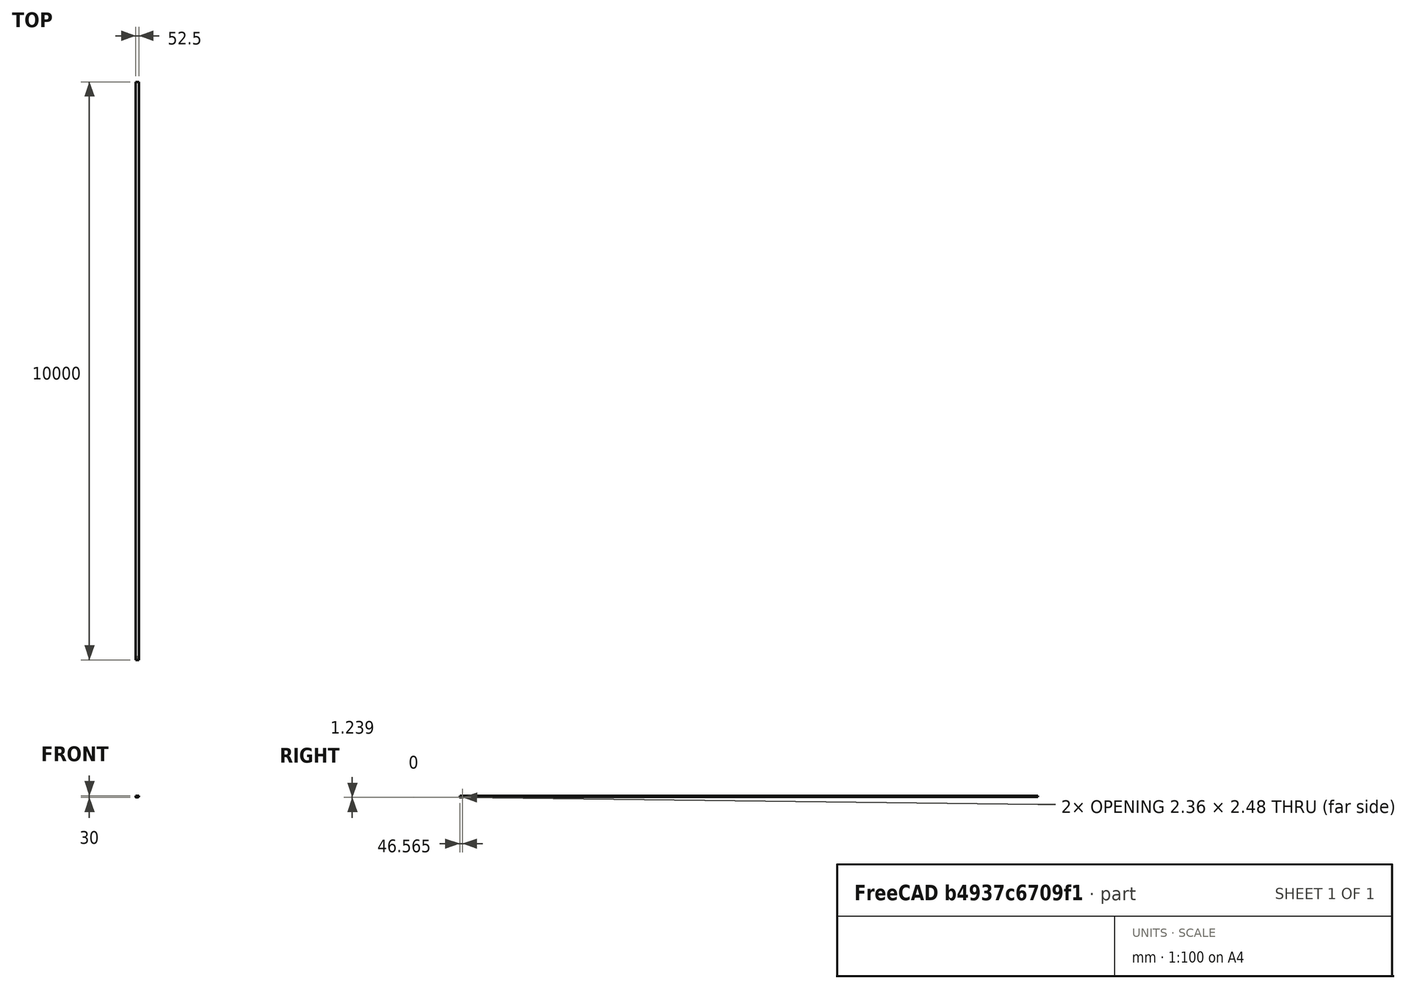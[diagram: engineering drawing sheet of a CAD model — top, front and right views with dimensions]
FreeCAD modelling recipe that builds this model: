
FCSTD DOCUMENT  (FreeCAD 0.14R3700 (Git))
Label: Phone_stand_flippable_stand
License: CC-BY 3.0
LicenseURL: http://creativecommons.org/licenses/by/3.0/
objects: Sketcher::SketchObject×4, PartDesign::Pad×2, PartDesign::Pocket×2, PartDesign::Fillet×1, Mesh::Feature×1
note: 13 computed .brp shape members not serialized (recipe doc carries the construction recipe); baked Part::Feature solids carry a one-line shape summary decoded from their .brp

FEATURE [Sketcher::SketchObject] Sketch001  label="X-Section"
  Placement = pos=(0,0,0) rot=(0.57735,0.57735,0.57735;2.0944rad)
  sketch-geometry (13):
    g0: LineSegment StartX=1.5 StartY=0 StartZ=0 EndX=58 EndY=0 EndZ=0
    g1: LineSegment StartX=58 StartY=4 StartZ=0 EndX=5.5 EndY=4 EndZ=0
    g2: LineSegment StartX=0 StartY=16.2 StartZ=0 EndX=0 EndY=1.5 EndZ=0
    g3: LineSegment StartX=1.5 StartY=17.7 StartZ=0 EndX=6.23478 EndY=17.7 EndZ=0
    g4: ArcOfCircle CenterX=1.5 CenterY=1.5 CenterZ=0 NormalX=0 NormalY=0 NormalZ=1 Radius=1.5 StartAngle=3.14159 EndAngle=4.71239
    g5: ArcOfCircle CenterX=1.5 CenterY=16.2 CenterZ=0 NormalX=0 NormalY=0 NormalZ=1 Radius=1.5 StartAngle=1.5708 EndAngle=3.14159
    g6: LineSegment StartX=4 StartY=5.5 StartZ=0 EndX=4 EndY=12.8 EndZ=0
    g7: ArcOfCircle CenterX=6.23116 CenterY=12.8 CenterZ=0 NormalX=0 NormalY=0 NormalZ=1 Radius=2.23116 StartAngle=2.27529 EndAngle=3.14159
    g8: LineSegment StartX=4.78615 StartY=14.5 StartZ=0 EndX=6.78615 EndY=16.2 EndZ=0
    g9: ArcOfCircle CenterX=6.23478 CenterY=16.8487 CenterZ=0 NormalX=0 NormalY=0 NormalZ=1 Radius=0.851335 StartAngle=5.41688 EndAngle=7.85398
    g10: LineSegment [constr] StartX=0 StartY=16.2 StartZ=0 EndX=6.78615 EndY=16.2 EndZ=0
    g11: LineSegment StartX=58 StartY=4 StartZ=0 EndX=58 EndY=0 EndZ=0
    g12: ArcOfCircle CenterX=5.5 CenterY=5.5 CenterZ=0 NormalX=0 NormalY=0 NormalZ=1 Radius=1.5 StartAngle=3.14159 EndAngle=4.71239
  constraints (36):
    c: Horizontal(g0)
    c: Horizontal(g1)
    c: Vertical(g2)
    c: Horizontal(g3)
    c: Tangent(g2,g4)
    c: Tangent(g0,g4)
    c: Tangent(g2,g5)
    c: Tangent(g3,g5)
    c: PointOnObject(g2,g-2)
    c: Vertical(g6)
    c: Coincident(g7,g6)
    c: Tangent(g7,g6)
    c: Coincident(g8,g7)
    c: Tangent(g8,g7)
    c: Tangent(g8,g9)
    c: Coincident(g9,g3)
    c: Tangent(g3,g9)
    c: Coincident(g10,g2)
    c: Coincident(g10,g8)
    c: Horizontal(g10)
    c: Radius(g4) = 1.5
    c: Radius(g5) = 1.5
    c: PointOnObject(g0,g-1)
    c: DistanceX(g7,g8) = 2
    c: Coincident(g11,g1)
    c: Coincident(g11,g0)
    c: Vertical(g11)
    c: DistanceY(g11) = -4
    c: DistanceX(g2,g0) = 58
    c: Tangent(g1,g12)
    c: Tangent(g6,g12)
    c: DistanceX(g6,g2) = -4
    c: DistanceY(g6,g1) = -8.8
    c: DistanceY(g7,g1) = -10.5
    c: DistanceY(g8,g1) = -12.2
    c: Radius(g12) = 1.5
FEATURE [PartDesign::Pad] Pad
  Length = 40
  Length2 = 100
  Placement = pos=(0,0,0) rot=(0.57735,0.57735,0.57735;2.0944rad)
  Sketch = -> Sketch001
  Type = 0
FEATURE [Sketcher::SketchObject] Sketch  label="Centre-Pocket"
  ExternalGeometry = -> [Pad]
  Placement = pos=(0,0,0) rot=(0.707107,0.707107,0;3.14159rad)
  Support = -> Pad [Face4]
  sketch-geometry (7):
    g0: LineSegment StartX=0 StartY=30 StartZ=0 EndX=52.5 EndY=30 EndZ=0
    g1: LineSegment StartX=52.5 StartY=30 StartZ=0 EndX=52.5 EndY=10 EndZ=0
    g2: LineSegment StartX=52.5 StartY=10 StartZ=0 EndX=0 EndY=10 EndZ=0
    g3: LineSegment StartX=0 StartY=10 StartZ=0 EndX=0 EndY=30 EndZ=0
    g4: LineSegment [constr] StartX=0 StartY=20 StartZ=0 EndX=58 EndY=20 EndZ=0
    g5: LineSegment [constr] StartX=1.5 StartY=40 StartZ=0 EndX=46.5 EndY=40 EndZ=0
    g6: LineSegment [constr] StartX=46.5 StartY=40 StartZ=0 EndX=52.5 EndY=40 EndZ=0
  constraints (20):
    c: Coincident(g0,g1)
    c: Coincident(g1,g2)
    c: Coincident(g2,g3)
    c: Coincident(g3,g0)
    c: Horizontal(g0)
    c: Horizontal(g2)
    c: Vertical(g1)
    c: Vertical(g3)
    c: Symmetric(g0,g2,g4)
    c: PointOnObject(g4,g-2)
    c: DistanceY(g3) = 20
    c: PointOnObject(g4,g3)
    c: Horizontal(g5)
    c: DistanceX(g5) = 45
    c: Symmetric(g-3,g-3,g4)
    c: Coincident(g6,g5)
    c: Horizontal(g6)
    c: DistanceX(g6) = 6
    c: PointOnObject(g6,g1)
    c: Coincident(g5,g-4)
FEATURE [PartDesign::Pocket] Pocket
  Length = 5
  Placement = pos=(0,0,0) rot=(0.57735,0.57735,0.57735;2.0944rad)
  Sketch = -> Sketch
  Type = 1
FEATURE [Sketcher::SketchObject] Sketch002  label="Centre-Hinge-X-Section"
  ExternalGeometry = -> [Pocket]
  Placement = pos=(10,0,0) rot=(0.57735,0.57735,0.57735;2.0944rad)
  Support = -> Pocket [Face4]
  sketch-geometry (12):
    g0: LineSegment [constr] StartX=1.5 StartY=1.5 StartZ=0 EndX=46.5 EndY=1.5 EndZ=0
    g1: LineSegment StartX=52.5 StartY=4 StartZ=0 EndX=51 EndY=4 EndZ=0
    g2: LineSegment StartX=52.5 StartY=4 StartZ=0 EndX=52.5 EndY=0 EndZ=0
    g3: LineSegment StartX=52.5 StartY=0 StartZ=0 EndX=51.866 EndY=0 EndZ=0
    g4: LineSegment StartX=51 StartY=4 StartZ=0 EndX=51 EndY=1.5 EndZ=0
    g5: LineSegment StartX=51 StartY=1.5 StartZ=0 EndX=51.866 EndY=0 EndZ=0
    g6: ArcOfCircle CenterX=1.5 CenterY=1.5 CenterZ=0 NormalX=0 NormalY=0 NormalZ=1 Radius=1.5 StartAngle=2.15007 EndAngle=6.75111
    g7: LineSegment StartX=0.678881 StartY=2.75529 StartZ=0 EndX=2.83876 EndY=2.17656 EndZ=0
    g8: ArcOfCircle CenterX=46.5 CenterY=1.25 CenterZ=0 NormalX=0 NormalY=0 NormalZ=1 Radius=1.25 StartAngle=3.61116 EndAngle=8.03975
    g9: LineSegment StartX=46.2691 StartY=2.47849 StartZ=0 EndX=45.3853 EndY=0.684378 EndZ=0
    g10: LineSegment [constr] StartX=51.866 StartY=0 StartZ=0 EndX=43.7463 EndY=4 EndZ=0
    g11: LineSegment [constr] StartX=46.5 StartY=1.5 StartZ=0 EndX=46.5 EndY=1.25 EndZ=0
  constraints (36):
    c: Horizontal(g0)
    c: DistanceX(g0) = 45
    c: Horizontal(g1)
    c: Coincident(g2,g1)
    c: Vertical(g2)
    c: Coincident(g3,g2)
    c: Horizontal(g3)
    c: Coincident(g4,g1)
    c: Vertical(g4)
    c: Coincident(g5,g4)
    c: Coincident(g5,g3)
    c: Angle(g5) = -1.0472
    c: PointOnObject(g4,g0)
    c: DistanceX(g0) = 1.5
    c: DistanceY(g0) = 1.5
    c: Coincident(g6,g0)
    c: Coincident(g7,g6)
    c: Coincident(g6,g7)
    c: Radius(g6) = 1.5
    c: DistanceX(g0,g1) = 4.5
    c: Radius(g8) = 1.25
    c: Coincident(g9,g8)
    c: Coincident(g9,g8)
    c: Coincident(g10,g3)
    c: Tangent(g10,g8)
    c: PointOnObject(g10,g1)
    c: Perpendicular(g9,g10)
    c: Coincident(g1,g-3)
    c: Coincident(g2,g-3)
    c: Distance(g0,g7) = 1
    c: Angle(g7) = -0.261799
    c: Distance(g8,g9) = 0.75
    c: Coincident(g11,g0)
    c: Coincident(g11,g8)
    c: Vertical(g11)
    c: DistanceY(g11) = -0.25
FEATURE [PartDesign::Pad] Pad001
  Length = 4
  Length2 = 100
  Placement = pos=(0,0,0) rot=(0.57735,0.57735,0.57735;2.0944rad)
  Sketch = -> Sketch002
  Type = 2
FEATURE [Sketcher::SketchObject] Sketch003
  ExternalGeometry = -> [Pad001]
  Placement = pos=(0,0,17.7) rot=(0,0,-1;1.5708rad)
  Support = -> Pad001 [Face5]
  sketch-geometry (6):
    g0: LineSegment StartX=-2.99999 StartY=40 StartZ=0 EndX=2 EndY=40 EndZ=0
    g1: LineSegment StartX=2 StartY=40 StartZ=0 EndX=2 EndY=35 EndZ=0
    g2: LineSegment StartX=-3 StartY=0 StartZ=0 EndX=2 EndY=0 EndZ=0
    g3: LineSegment StartX=2 StartY=0 StartZ=0 EndX=2 EndY=5 EndZ=0
    g4: ArcOfCircle CenterX=-3 CenterY=5 CenterZ=0 NormalX=0 NormalY=0 NormalZ=1 Radius=5 StartAngle=4.71239 EndAngle=6.28319
    g5: ArcOfCircle CenterX=-3 CenterY=35 CenterZ=0 NormalX=0 NormalY=0 NormalZ=1 Radius=5 StartAngle=6.28318 EndAngle=7.85398
FEATURE [PartDesign::Pocket] Pocket001
  Length = 5
  Placement = pos=(0,0,0) rot=(0.57735,0.57735,0.57735;2.0944rad)
  Sketch = -> Sketch003
  Type = 1
FEATURE [PartDesign::Fillet] Fillet
  Base = -> Pocket001 [Edge43,Edge78]
  Placement = pos=(0,0,0) rot=(0.57735,0.57735,0.57735;2.0944rad)
  Radius = 5
FEATURE [Mesh::Feature] Mesh  label="Fillet (Meshed)"
